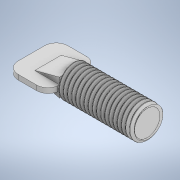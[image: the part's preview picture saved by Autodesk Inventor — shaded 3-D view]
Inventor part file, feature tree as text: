
AUTODESK INVENTOR PART (.ipt)
format: ipt  version: 2020 (Build 240168000, 168)  size: 1,179,648 bytes
history: native  units: mm
features: sketch x6, extrude x3, chamfer x2, revolve x2, fillet x1, thread x1, helix x1
ambient origin geometry x8: Origin, YZ Plane, XZ Plane, XY Plane, X Axis, Y Axis, Z Axis, Center Point
bodies: Solid1 (feature_tree), Solid7 (feature_tree)
feature tree (16):
  extrude  "Extrusion1"  Depth=45.0mm TaperAngle=0.0deg
  extrude  "Extrusion2"  Depth=3.0mm
  extrude  "Extrusion3"  Depth=16.0mm
  chamfer  "Chamfer1"  Distance=15.0mm
  chamfer  "Chamfer2"  Distance=4.0mm Angle=45.0deg
  fillet  "Fillet1"  Radius=4.0mm
  thread  "Thread9"  [1 undecoded]
  revolve  "Revolution11"  [1 undecoded]
  revolve  "Revolution12"  [1 undecoded]
  helix  "Coil6"  [1 undecoded]
  sketch  "Sketch1"  dims[d0=19.0mm d1=45.0mm d2=0.0mm]
  sketch  "Sketch3"  dims[d5=30.0mm d6=3.0mm]
  sketch  "Sketch4"  dims[d7=25.0mm d8=0.0mm d9=16.0mm]
  sketch  "Sketch21"  dims[d10=4.0mm]
  sketch  "Sketch22"  dims[d11=16.0mm]
  sketch  "Sketch23"  dims[d12=4.0mm d13=15.0mm d14=0.0mm d15=4.0mm d16=15.0mm d17=45.0deg d18=4.0mm d19=15.0mm d20=45.0deg d21=7.0mm d33=9.599311mm d54=9.599311mm d75=9.599311mm d96=9.599311mm d119=9.599311mm d131=45.0mm d132=0.0mm d133=9.599311mm d134=0.400208mm d135=0.400208mm d138=2.5mm d140=9.599311mm d142=0.0mm d143=0.0mm d144=2.5025mm d145=50.0mm d146=10.0mm d147=0.0mm d148=0.0mm d149=0.0mm d150=0.0mm d151=0.0mm]
note: 4 required parameter values undecoded (feature->parameter linkage not recoverable at this tier; creation-order binding heuristic only, values carry confidence <= 0.55)